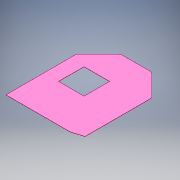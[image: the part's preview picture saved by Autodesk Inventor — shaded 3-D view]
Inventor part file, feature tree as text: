
AUTODESK INVENTOR PART (.ipt)
format: ipt  version: 2018 (Build 220112000, 112)  size: 145,408 bytes
history: native  units: mm
features: extrude x1, fillet x1, sketch x1
ambient origin geometry x8: Origin, YZ Plane, XZ Plane, XY Plane, X Axis, Y Axis, Z Axis, Center Point
bodies: Solid1 (feature_tree)
feature tree (3):
  extrude  "Extrusion1"  Depth=220.0mm
  fillet  "Fillet1"  Radius=220.0mm
  sketch  "Sketch1"  dims[d10=110.0mm d11=220.0mm d12=220.0mm d13=1.6mm d14=0.0mm d21=100.0mm d24=550.0mm d25=126.0mm d29=30.0mm d30=270.0mm d31=135.0deg d32=270.0mm d33=45.0deg d34=605.0mm d35=250.0mm d36=30.0mm]
